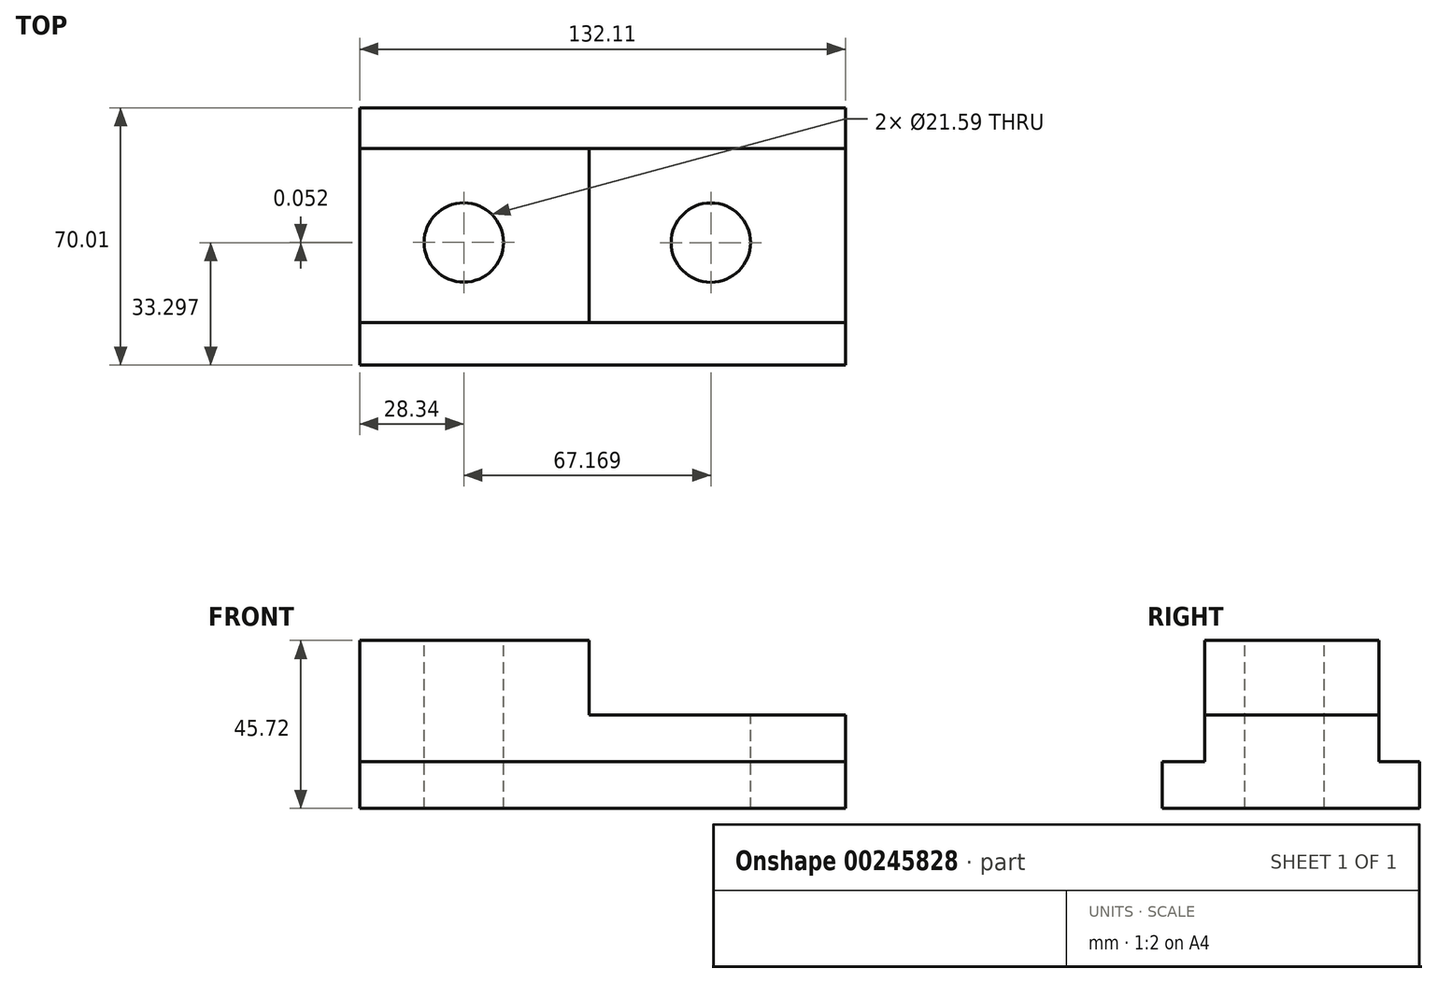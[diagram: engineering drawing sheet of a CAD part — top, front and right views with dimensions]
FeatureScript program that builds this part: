
annotation { "Feature Type Name" : "Feature", "Feature Type Description" : "" }
export const myFeature = defineFeature(function(context is Context, id is Id, definition is map)
    precondition{}
    {
        {
            var Q0;
            Q0=qCreatedBy(makeId("Top.planeOp"),FACE);
            var sketch = newSketch(context, id + "F0", { "sketchPlane" : qUnion([Q0])});
            skLineSegment(sketch, "E0.bottom", {"start": v(-72.92, 30.7) * mm, "end": v(59.2, 30.7) * mm});
            skLineSegment(sketch, "E0.top", {"start": v(-72.92, -39.3) * mm, "end": v(59.2, -39.3) * mm});
            skLineSegment(sketch, "E0.left", {"start": v(-72.92, 30.7) * mm, "end": v(-72.92, -39.3) * mm});
            skLineSegment(sketch, "E0.right", {"start": v(59.2, 30.7) * mm, "end": v(59.2, -39.3) * mm});
            skSolve(sketch);
        }
        {
            var Q0;
            Q0=makeQuery(id+"F0.imprint","IMPRINT",FACE,{"disambiguationData":[TD([[makeQuery(id+"F0.imprint","IMPRINT",EDGE,{"derivedFrom":sQuery(id+"F0.wireOp",EDGE,"E0.bottom")}),-1.0]])]});
            extrude(context, id + "F1", {"entities" : qUnion([Q0]), "depth" : 25.4 * mm});
        }
        {
            var Q0;
            Q0=makeQuery(id+"F1.opExtrude","CAP_FACE",FACE,{"disambiguationData":[OSD([sQuery(id+"F0.wireOp",EDGE,"E0.bottom"),sQuery(id+"F0.wireOp",EDGE,"E0.top"),sQuery(id+"F0.wireOp",EDGE,"E0.left"),sQuery(id+"F0.wireOp",EDGE,"E0.right")])],"isStart":false});
            var sketch = newSketch(context, id + "F2", { "sketchPlane" : qUnion([Q0])});
            skLineSegment(sketch, "E1.bottom", {"start": v(-72.92, -39.3) * mm, "end": v(59.2, -39.3) * mm});
            skLineSegment(sketch, "E1.top", {"start": v(-72.92, -27.7) * mm, "end": v(59.2, -27.7) * mm});
            skLineSegment(sketch, "E1.left", {"start": v(-72.92, -39.3) * mm, "end": v(-72.92, -27.7) * mm});
            skLineSegment(sketch, "E1.right", {"start": v(59.2, -39.3) * mm, "end": v(59.2, -27.7) * mm});
            skSolve(sketch);
        }
        {
            var Q0;
            Q0=makeQuery(id+"F2.imprint","IMPRINT",FACE,{"disambiguationData":[TD([[makeQuery(id+"F2.imprint","IMPRINT",EDGE,{"derivedFrom":sQuery(id+"F2.wireOp",EDGE,"E1.bottom")}),1.0]])]});
            extrude(context, id + "F3", {"entities" : qUnion([Q0]), "operationType" : NewBodyOperationType.REMOVE, "oppositeDirection" : true, "depth" : 12.7 * mm});
        }
        {
            var Q0;
            Q0=makeQuery(id+"F1.opExtrude","CAP_FACE",FACE,{"disambiguationData":[OSD([sQuery(id+"F0.wireOp",EDGE,"E0.bottom"),sQuery(id+"F0.wireOp",EDGE,"E0.top"),sQuery(id+"F0.wireOp",EDGE,"E0.left"),sQuery(id+"F0.wireOp",EDGE,"E0.right")])],"isStart":false});
            var sketch = newSketch(context, id + "F4", { "sketchPlane" : qUnion([Q0])});
            skLineSegment(sketch, "E2.bottom", {"start": v(59.2, 30.7) * mm, "end": v(-72.92, 30.7) * mm});
            skLineSegment(sketch, "E2.top", {"start": v(59.2, 19.64) * mm, "end": v(-72.92, 19.64) * mm});
            skLineSegment(sketch, "E2.left", {"start": v(59.2, 30.7) * mm, "end": v(59.2, 19.64) * mm});
            skLineSegment(sketch, "E2.right", {"start": v(-72.92, 30.7) * mm, "end": v(-72.92, 19.64) * mm});
            skSolve(sketch);
        }
        {
            var Q0;
            Q0=makeQuery(id+"F4.imprint","IMPRINT",FACE,{"disambiguationData":[TD([[makeQuery(id+"F4.imprint","IMPRINT",EDGE,{"derivedFrom":sQuery(id+"F4.wireOp",EDGE,"E2.bottom")}),-1.0]])]});
            extrude(context, id + "F5", {"entities" : qUnion([Q0]), "operationType" : NewBodyOperationType.REMOVE, "oppositeDirection" : true, "depth" : 12.7 * mm});
        }
        {
            var Q0;
            Q0=makeQuery(id+"F1.opExtrude","CAP_FACE",FACE,{"disambiguationData":[OSD([sQuery(id+"F0.wireOp",EDGE,"E0.bottom"),sQuery(id+"F0.wireOp",EDGE,"E0.top"),sQuery(id+"F0.wireOp",EDGE,"E0.left"),sQuery(id+"F0.wireOp",EDGE,"E0.right")])],"isStart":false});
            var sketch = newSketch(context, id + "F6", { "sketchPlane" : qUnion([Q0])});
            skLineSegment(sketch, "E3.bottom", {"start": v(-72.92, -27.7) * mm, "end": v(-10.5, -27.7) * mm});
            skLineSegment(sketch, "E3.top", {"start": v(-72.92, 19.64) * mm, "end": v(-10.5, 19.64) * mm});
            skLineSegment(sketch, "E3.left", {"start": v(-72.92, -27.7) * mm, "end": v(-72.92, 19.64) * mm});
            skLineSegment(sketch, "E3.right", {"start": v(-10.5, -27.7) * mm, "end": v(-10.5, 19.64) * mm});
            skSolve(sketch);
        }
        {
            var Q0;
            Q0=makeQuery(id+"F6.imprint","IMPRINT",FACE,{"disambiguationData":[TD([[makeQuery(id+"F6.imprint","IMPRINT",EDGE,{"derivedFrom":sQuery(id+"F6.wireOp",EDGE,"E3.bottom")}),1.0]])]});
            extrude(context, id + "F7", {"entities" : qUnion([Q0]), "operationType" : NewBodyOperationType.ADD, "depth" : 20.32 * mm});
        }
        {
            var Q0;
            Q0=makeQuery(id+"F7.opExtrude","CAP_FACE",FACE,{"disambiguationData":[OSD([sQuery(id+"F6.wireOp",EDGE,"E3.bottom"),sQuery(id+"F6.wireOp",EDGE,"E3.top"),sQuery(id+"F6.wireOp",EDGE,"E3.left"),sQuery(id+"F6.wireOp",EDGE,"E3.right")])],"isStart":false});
            var sketch = newSketch(context, id + "F8", { "sketchPlane" : qUnion([Q0])});
            skCircle(sketch, "E4", {"center": v(-44.58, -5.96) * mm, "radius": 10.02 * mm});
            skSolve(sketch);
        }
        {
            var Q0;
            Q0=makeQuery(id+"F1.opExtrude","CAP_FACE",FACE,{"disambiguationData":[OSD([sQuery(id+"F0.wireOp",EDGE,"E0.bottom"),sQuery(id+"F0.wireOp",EDGE,"E0.top"),sQuery(id+"F0.wireOp",EDGE,"E0.left"),sQuery(id+"F0.wireOp",EDGE,"E0.right")])],"isStart":false});
            var sketch = newSketch(context, id + "F9", { "sketchPlane" : qUnion([Q0])});
            skCircle(sketch, "E5", {"center": v(22.59, -6.01) * mm, "radius": 10.51 * mm});
            skSolve(sketch);
        }
        {
            var Q0;
            Q0=sQuery(id+"F8.wireOp",VERTEX,"E4.center");
            var Q1;
            Q1=makeQuery(id+"F1.opExtrude","SWEPT_BODY",BODY,{"disambiguationData":[OSD([sQuery(id+"F0.wireOp",EDGE,"E0.bottom"),sQuery(id+"F0.wireOp",EDGE,"E0.top"),sQuery(id+"F0.wireOp",EDGE,"E0.left"),sQuery(id+"F0.wireOp",EDGE,"E0.right")])]});
            hole(context, id + "F10", {"style" : HoleStyle.SIMPLE, "endStyle" : HoleEndStyle.THROUGH, "holeDiameter" : 21.59 * mm, "tappedDepth" : 12.7 * mm, "tapClearance" : 3, "locations" : qUnion([Q0]), "scope" : qUnion([Q1])});
        }
        {
            var Q0;
            Q0=makeQuery(id+"F9.imprint","IMPRINT",FACE,{"disambiguationData":[TD([[makeQuery(id+"F9.imprint","IMPRINT",EDGE,{"derivedFrom":sQuery(id+"F9.wireOp",EDGE,"E5")}),-1.0]])]});
            var sketch = newSketch(context, id + "F11", { "sketchPlane" : qUnion([Q0])});
            skLineSegment(sketch, "E6", {"start": v(22.59, -6.01) * mm, "end": v(22.59, 42.1) * mm});
            skLineSegment(sketch, "E7", {"start": v(22.59, -6.01) * mm, "end": v(18.04, -46.4) * mm});
            skLineSegment(sketch, "E8", {"start": v(22.59, -6.01) * mm, "end": v(58.9, -10.1) * mm});
            skLineSegment(sketch, "E9", {"start": v(22.59, -6.01) * mm, "end": v(-2.64, -6.01) * mm});
            skSolve(sketch);
        }
        {
            var Q0;
            Q0=sQuery(id+"F11.wireOp",VERTEX,"E9.start");
            var Q1;
            Q1=makeQuery(id+"F1.opExtrude","SWEPT_BODY",BODY,{"disambiguationData":[OSD([sQuery(id+"F0.wireOp",EDGE,"E0.bottom"),sQuery(id+"F0.wireOp",EDGE,"E0.top"),sQuery(id+"F0.wireOp",EDGE,"E0.left"),sQuery(id+"F0.wireOp",EDGE,"E0.right")])]});
            hole(context, id + "F12", {"style" : HoleStyle.SIMPLE, "endStyle" : HoleEndStyle.THROUGH, "holeDiameter" : 21.59 * mm, "tappedDepth" : 12.7 * mm, "tapClearance" : 3, "locations" : qUnion([Q0]), "scope" : qUnion([Q1])});
        }
    });
